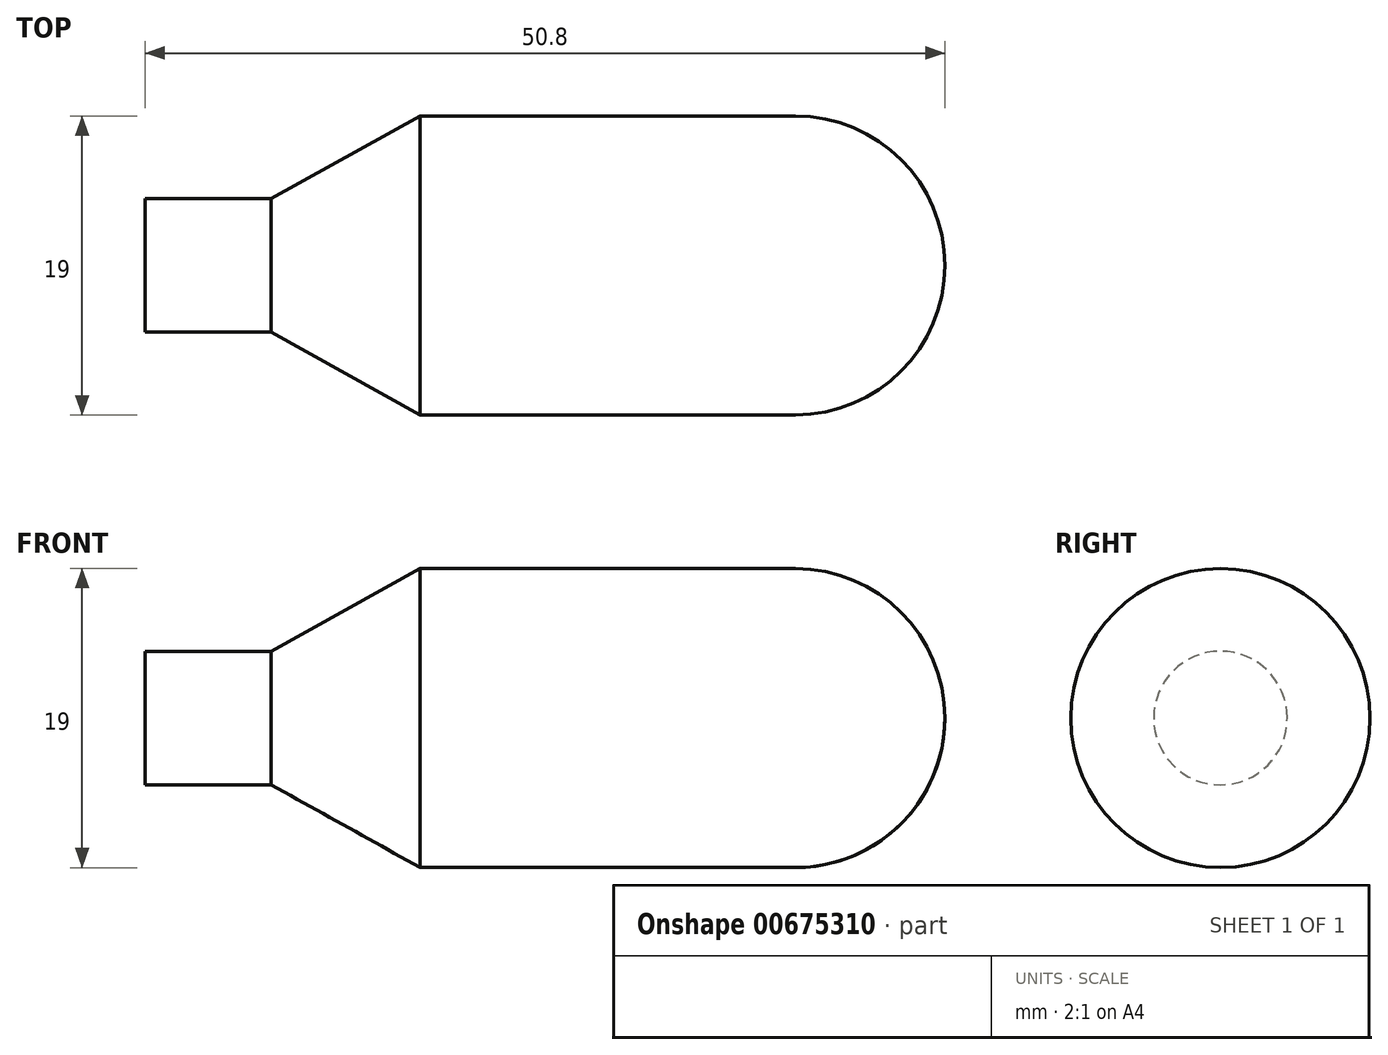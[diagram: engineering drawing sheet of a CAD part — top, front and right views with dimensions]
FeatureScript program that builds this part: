
annotation { "Feature Type Name" : "Feature", "Feature Type Description" : "" }
export const myFeature = defineFeature(function(context is Context, id is Id, definition is map)
    precondition{}
    {
        {
            var Q0;
            Q0=qCreatedBy(makeId("Front.planeOp"),FACE);
            var sketch = newSketch(context, id + "F0", { "sketchPlane" : qUnion([Q0])});
            skLineSegment(sketch, "E0", {"start": v(-5.62, 0) * mm, "end": v(-5.62, 4.24) * mm});
            skLineSegment(sketch, "E1", {"start": v(-5.62, 4.24) * mm, "end": v(2.38, 4.24) * mm});
            skLineSegment(sketch, "E2", {"start": v(11.86, 9.5) * mm, "end": v(35.68, 9.5) * mm});
            skLineSegment(sketch, "E3", {"start": v(45.18, 0) * mm, "end": v(45.18, 0) * mm});
            skLineSegment(sketch, "E4", {"start": v(45.18, 0) * mm, "end": v(-5.62, 0) * mm});
            skLineSegment(sketch, "E5", {"start": v(2.38, 4.24) * mm, "end": v(11.86, 9.5) * mm});
            skPoint(sketch, "E6.visualSharp", {"position": v(45.18, 9.5) * mm});
            skArc(sketch, "E6.filletArc", {"start": v(45.18, 0) * mm, "mid": v(42.4, 6.72) * mm, "end": v(35.68, 9.5) * mm});
            skSolve(sketch);
        }
        {
            var Q0;
            Q0=makeQuery(id+"F0.imprint","IMPRINT",FACE,{"disambiguationData":[TD([[makeQuery(id+"F0.imprint","IMPRINT",EDGE,{"derivedFrom":sQuery(id+"F0.wireOp",EDGE,"E0")}),-1.0]])]});
            var Q1;
            Q1=sQuery(id+"F0.wireOp",EDGE,"E4");
            revolve(context, id + "F1", {"surfaceOperationType" : NewSurfaceOperationType.NEW, "entities" : qUnion([Q0]), "axis" : qUnion([Q1]), "revolveType" : RevolveType.FULL});
        }
    });
